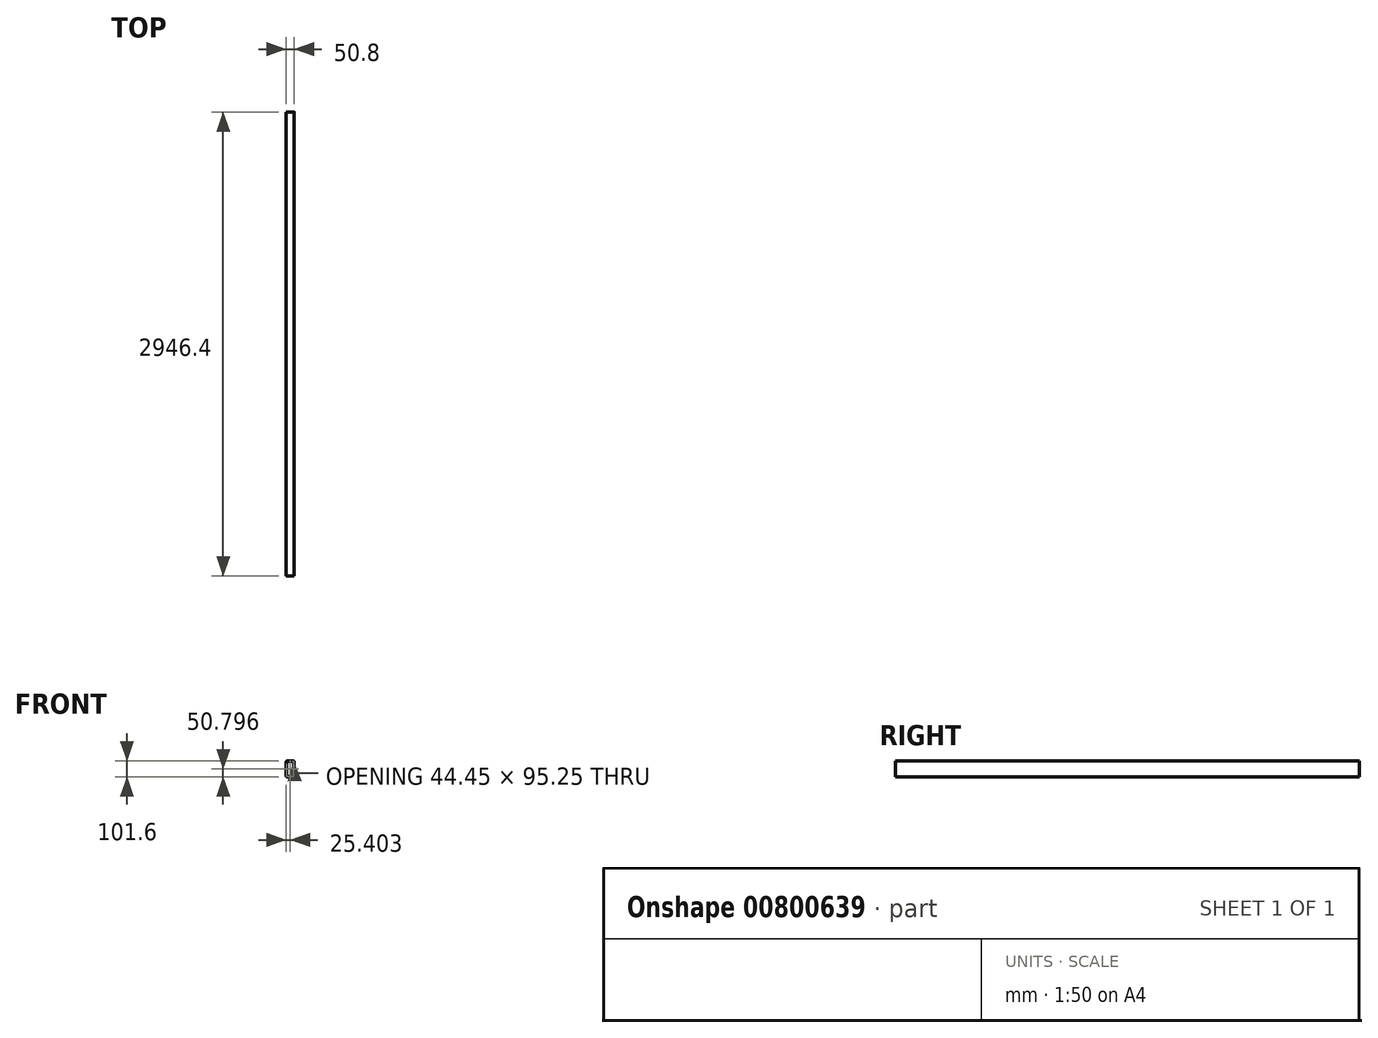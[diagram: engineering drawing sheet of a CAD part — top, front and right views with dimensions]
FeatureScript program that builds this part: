
annotation { "Feature Type Name" : "Feature", "Feature Type Description" : "" }
export const myFeature = defineFeature(function(context is Context, id is Id, definition is map)
    precondition{}
    {
        {
            var Q0;
            Q0=qCreatedBy(makeId("Front.planeOp"),FACE);
            var sketch = newSketch(context, id + "F0", { "sketchPlane" : qUnion([Q0])});
            skLineSegment(sketch, "E0.bottom", {"start": v(-21.77, 3.9) * mm, "end": v(-59.87, 3.9) * mm});
            skLineSegment(sketch, "E0.top", {"start": v(-21.77, 105.5) * mm, "end": v(-59.87, 105.5) * mm});
            skLineSegment(sketch, "E0.left", {"start": v(-15.42, 10.26) * mm, "end": v(-15.42, 99.16) * mm});
            skLineSegment(sketch, "E0.right", {"start": v(-66.22, 10.26) * mm, "end": v(-66.22, 99.16) * mm});
            skPoint(sketch, "E0.middle", {"position": v(-40.82, 54.7) * mm});
            skLineSegment(sketch, "E1.bottom", {"start": v(-24.94, 7.08) * mm, "end": v(-56.7, 7.08) * mm});
            skLineSegment(sketch, "E1.top", {"start": v(-24.94, 102.33) * mm, "end": v(-56.7, 102.33) * mm});
            skLineSegment(sketch, "E1.left", {"start": v(-18.6, 13.43) * mm, "end": v(-18.6, 95.98) * mm});
            skLineSegment(sketch, "E1.right", {"start": v(-63.04, 13.43) * mm, "end": v(-63.04, 95.98) * mm});
            skPoint(sketch, "E2.visualSharp", {"position": v(-63.04, 7.08) * mm});
            skArc(sketch, "E2.filletArc", {"start": v(-63.04, 13.43) * mm, "mid": v(-61.18, 8.94) * mm, "end": v(-56.7, 7.08) * mm});
            skPoint(sketch, "E3.visualSharp", {"position": v(-18.6, 7.08) * mm});
            skArc(sketch, "E3.filletArc", {"start": v(-24.94, 7.08) * mm, "mid": v(-20.45, 8.94) * mm, "end": v(-18.6, 13.43) * mm});
            skPoint(sketch, "E4.visualSharp", {"position": v(-15.42, 3.9) * mm});
            skArc(sketch, "E4.filletArc", {"start": v(-21.77, 3.9) * mm, "mid": v(-17.28, 5.77) * mm, "end": v(-15.42, 10.26) * mm});
            skPoint(sketch, "E5.visualSharp", {"position": v(-66.22, 3.9) * mm});
            skArc(sketch, "E5.filletArc", {"start": v(-66.22, 10.26) * mm, "mid": v(-64.36, 5.77) * mm, "end": v(-59.87, 3.9) * mm});
            skPoint(sketch, "E6.visualSharp", {"position": v(-63.04, 102.33) * mm});
            skArc(sketch, "E6.filletArc", {"start": v(-56.7, 102.33) * mm, "mid": v(-61.18, 100.47) * mm, "end": v(-63.04, 95.98) * mm});
            skPoint(sketch, "E7.visualSharp", {"position": v(-66.22, 105.5) * mm});
            skArc(sketch, "E7.filletArc", {"start": v(-59.87, 105.5) * mm, "mid": v(-64.36, 103.65) * mm, "end": v(-66.22, 99.16) * mm});
            skPoint(sketch, "E8.visualSharp", {"position": v(-18.6, 102.33) * mm});
            skArc(sketch, "E8.filletArc", {"start": v(-18.6, 95.98) * mm, "mid": v(-20.45, 100.47) * mm, "end": v(-24.94, 102.33) * mm});
            skPoint(sketch, "E9.visualSharp", {"position": v(-15.42, 105.5) * mm});
            skArc(sketch, "E9.filletArc", {"start": v(-15.42, 99.16) * mm, "mid": v(-17.28, 103.65) * mm, "end": v(-21.77, 105.5) * mm});
            skSolve(sketch);
        }
        {
            var Q0;
            Q0 = qSketchRegion(id + "F0", true);
            extrude(context, id + "F1", {"entities" : qUnion([Q0]), "depth" : 2946.4 * mm, "offsetDistance" : 25.4 * mm});
        }
    });
